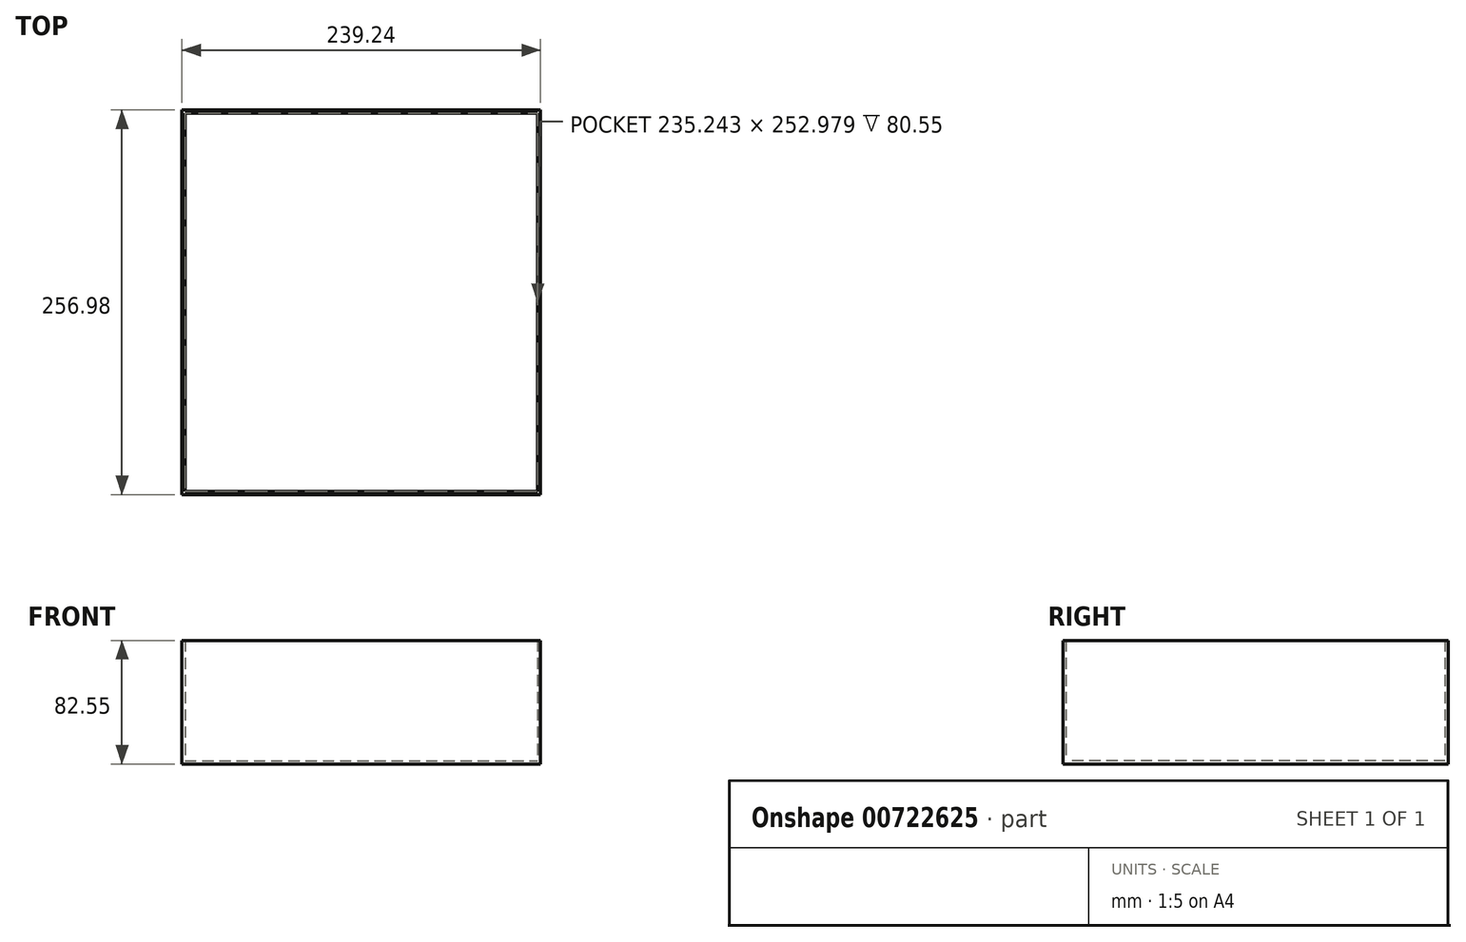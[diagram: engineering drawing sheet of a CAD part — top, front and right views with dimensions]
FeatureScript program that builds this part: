
annotation { "Feature Type Name" : "Feature", "Feature Type Description" : "" }
export const myFeature = defineFeature(function(context is Context, id is Id, definition is map)
    precondition{}
    {
        {
            var Q0;
            Q0=qCreatedBy(makeId("Top.planeOp"),FACE);
            var sketch = newSketch(context, id + "F0", { "sketchPlane" : qUnion([Q0])});
            skLineSegment(sketch, "E0.bottom", {"start": v(-145.41, 256.98) * mm, "end": v(93.83, 256.98) * mm});
            skLineSegment(sketch, "E0.top", {"start": v(-145.41, 0) * mm, "end": v(93.83, 0) * mm});
            skLineSegment(sketch, "E0.left", {"start": v(-145.41, 256.98) * mm, "end": v(-145.41, 0) * mm});
            skLineSegment(sketch, "E0.right", {"start": v(93.83, 256.98) * mm, "end": v(93.83, 0) * mm});
            skSolve(sketch);
        }
        {
            var Q0;
            Q0=makeQuery(id+"F0.imprint","IMPRINT",FACE,{"disambiguationData":[TD([[makeQuery(id+"F0.imprint","IMPRINT",EDGE,{"derivedFrom":sQuery(id+"F0.wireOp",EDGE,"E0.bottom")}),-1.0]])]});
            cPlane(context, id + "F1", {"entities" : qUnion([Q0]), "cplaneType" : CPlaneType.OFFSET, "offset" : 0 * mm, "width" : 152.4 * mm, "height" : 152.4 * mm});
        }
        {
            var Q0;
            Q0=makeQuery(id+"F0.imprint","IMPRINT",FACE,{"disambiguationData":[TD([[makeQuery(id+"F0.imprint","IMPRINT",EDGE,{"derivedFrom":sQuery(id+"F0.wireOp",EDGE,"E0.bottom")}),-1.0]])]});
            extrude(context, id + "F2", {"entities" : qUnion([Q0]), "depth" : 82.55 * mm, "offsetDistance" : 25.4 * mm});
        }
        {
            var Q0;
            Q0=makeQuery(id+"F2.opExtrude","CAP_FACE",FACE,{"disambiguationData":[OSD([sQuery(id+"F0.wireOp",EDGE,"E0.bottom"),sQuery(id+"F0.wireOp",EDGE,"E0.top"),sQuery(id+"F0.wireOp",EDGE,"E0.left"),sQuery(id+"F0.wireOp",EDGE,"E0.right")])],"isStart":false});
            var Q1;
            Q1=makeQuery(id+"F2.opExtrude","SWEPT_BODY",BODY,{"disambiguationData":[OSD([sQuery(id+"F0.wireOp",EDGE,"E0.bottom"),sQuery(id+"F0.wireOp",EDGE,"E0.top"),sQuery(id+"F0.wireOp",EDGE,"E0.left"),sQuery(id+"F0.wireOp",EDGE,"E0.right")])]});
            shell(context, id + "F3", {"entities" : qUnion([Q0]), "parts" : qUnion([Q1]), "thickness" : 2 * mm});
        }
        {
            var Q0;
            Q0 = qSketchRegion(id + "F0", true);
            extrude(context, id + "F4", {"entities" : qUnion([Q0]), "operationType" : NewBodyOperationType.ADD, "depth" : 2 * mm, "offsetDistance" : 25.4 * mm});
        }
    });
